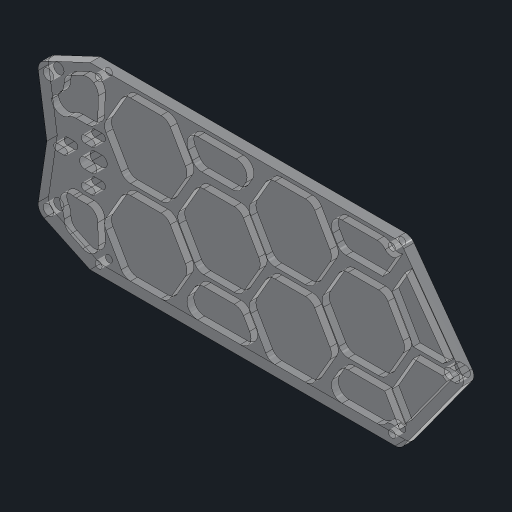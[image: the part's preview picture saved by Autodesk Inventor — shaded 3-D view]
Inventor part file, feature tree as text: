
AUTODESK INVENTOR PART (.ipt)
format: ipt  version: 2023.2 (Build 272271030, 271C)  size: 674,816 bytes
history: native  units: mm
features: extrude x4, sketch x3, projected_geometry x3, fillet x2, mirror x1
ambient origin geometry x8: Origin, YZ Plane, XZ Plane, XY Plane, X Axis, Y Axis, Z Axis, Center Point
bodies: Solid1 (feature_tree)
feature tree (13):
  extrude  "Extrusion1"  Depth=42.0mm
  extrude  "Extrusion2"  Depth=22.0mm
  extrude  "Extrusion3"  Depth=2.5mm
  mirror  "Mirror1"
  fillet  "Fillet2"  Radius=8.0mm
  extrude  "Extrusion5"  Depth=8.0mm
  fillet  "Fillet3"  Radius=4.0mm
  sketch  "Sketch1"  dims[d0=90.0mm d1=42.0mm]
  projected_geometry  "Projected Loop1"
  sketch  "Sketch3"  dims[d2=5.0mm d3=22.0mm]
  projected_geometry  "Projected Loop2"
  sketch  "Sketch5"  dims[d5=36.0mm d6=127.0mm d7=8.0mm d8=8.0mm d9=4.0mm d10=3.0mm d11=3.0mm d12=8.0mm d13=3.0mm d14=1.5mm d15=8.5mm d16=1.25mm d17=5.0mm d18=5.0mm d19=1.0mm d20=3.0mm d21=16.0mm d22=12.0mm d23=1.0mm d24=1.0mm d25=1.0mm d26=2.0mm d27=1.0mm d28=2.0mm d29=2.0mm d30=2.0mm d31=2.0mm d32=2.0mm d33=1.0mm d34=5.0mm d35=5.0mm d36=5.0mm d37=1.5mm d38=1.5mm d39=3.0mm d40=0.0mm d42=5.0mm d43=1.6mm d44=0.0mm d45=3.0mm d46=3.0mm d47=3.0mm d48=3.0mm d50=2.0mm d51=0.0mm d52=3.1mm d71=3.0mm d74=3.0mm d75=2.5mm d76=3.0mm d77=3.0mm d78=21.5mm d83=3.0mm d84=3.0mm d85=3.0mm d86=3.0mm d87=3.0mm d88=3.0mm d89=3.0mm d90=41.857895mm d91=30.0mm d93=41.857895mm d94=10.0mm d96=10.0mm d98=2.0mm d99=0.0mm d100=3.1mm d101=1.5mm d102=2.0mm d103=2.5mm d104=2.5mm d105=2.5mm d106=2.5mm d107=6.1mm]
  projected_geometry  "Projected Loop5"
